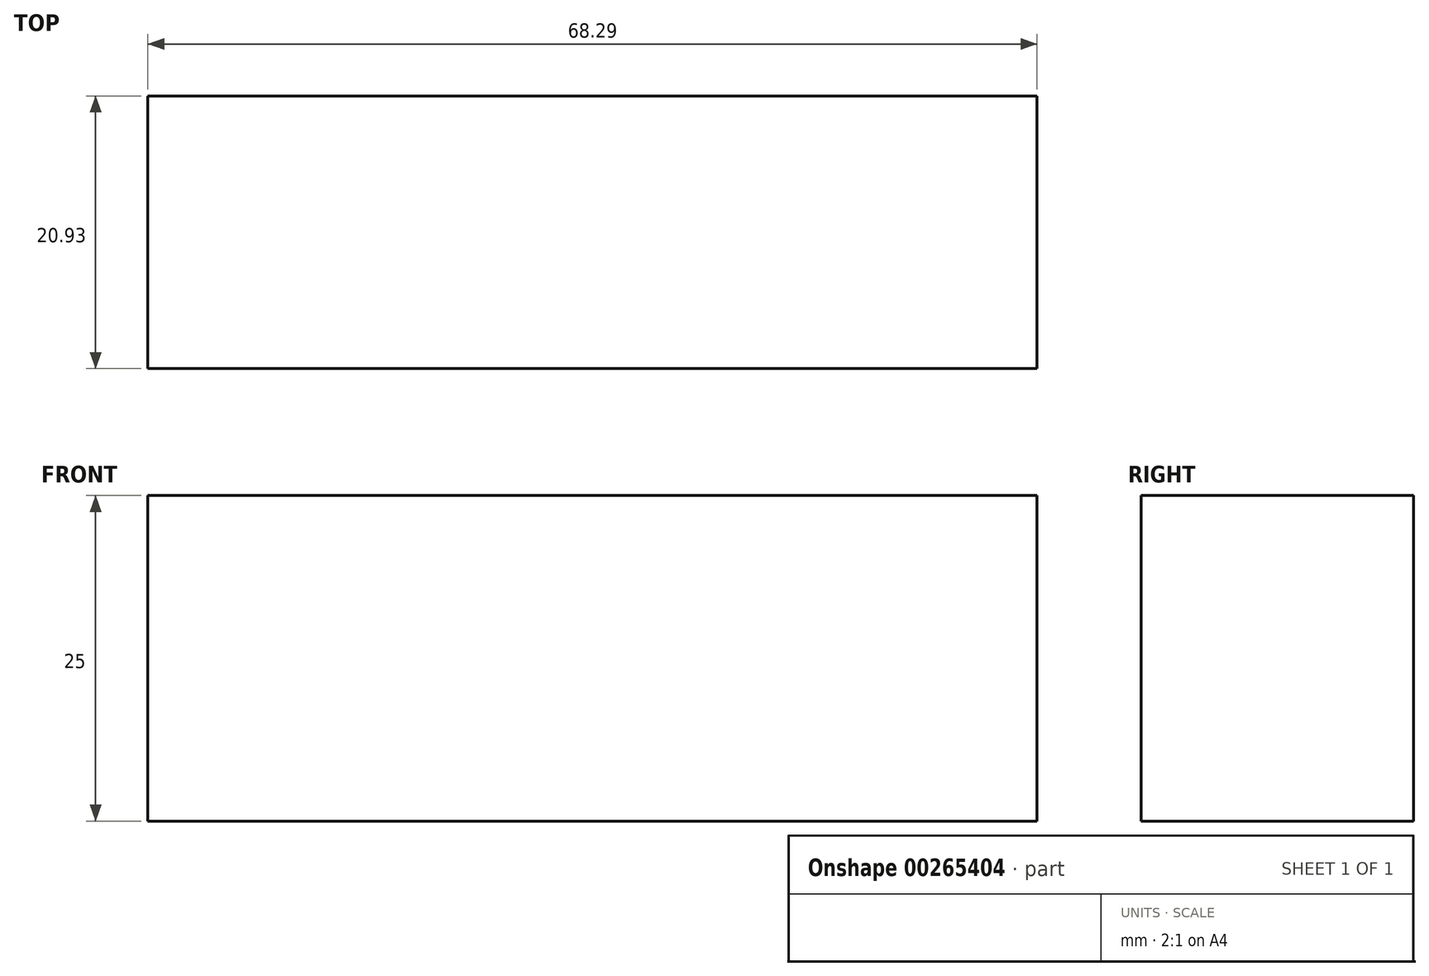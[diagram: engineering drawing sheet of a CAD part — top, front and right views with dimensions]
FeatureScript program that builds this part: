
annotation { "Feature Type Name" : "Feature", "Feature Type Description" : "" }
export const myFeature = defineFeature(function(context is Context, id is Id, definition is map)
    precondition{}
    {
        {
            var Q0;
            Q0=qCreatedBy(makeId("Top.planeOp"),FACE);
            var sketch = newSketch(context, id + "F0", { "sketchPlane" : qUnion([Q0])});
            skLineSegment(sketch, "E0", {"start": v(-40.2, -33.96) * mm, "end": v(28.09, -33.96) * mm});
            skLineSegment(sketch, "E1", {"start": v(28.09, -33.96) * mm, "end": v(28.09, -54.89) * mm});
            skLineSegment(sketch, "E2", {"start": v(28.09, -54.89) * mm, "end": v(-40.2, -54.89) * mm});
            skLineSegment(sketch, "E3", {"start": v(-40.2, -54.89) * mm, "end": v(-40.2, -33.96) * mm});
            skSolve(sketch);
        }
        {
            var Q0;
            Q0 = qSketchRegion(id + "F0", true);
            extrude(context, id + "F1", {"entities" : qUnion([Q0]), "depth" : 25 * mm});
        }
    });
